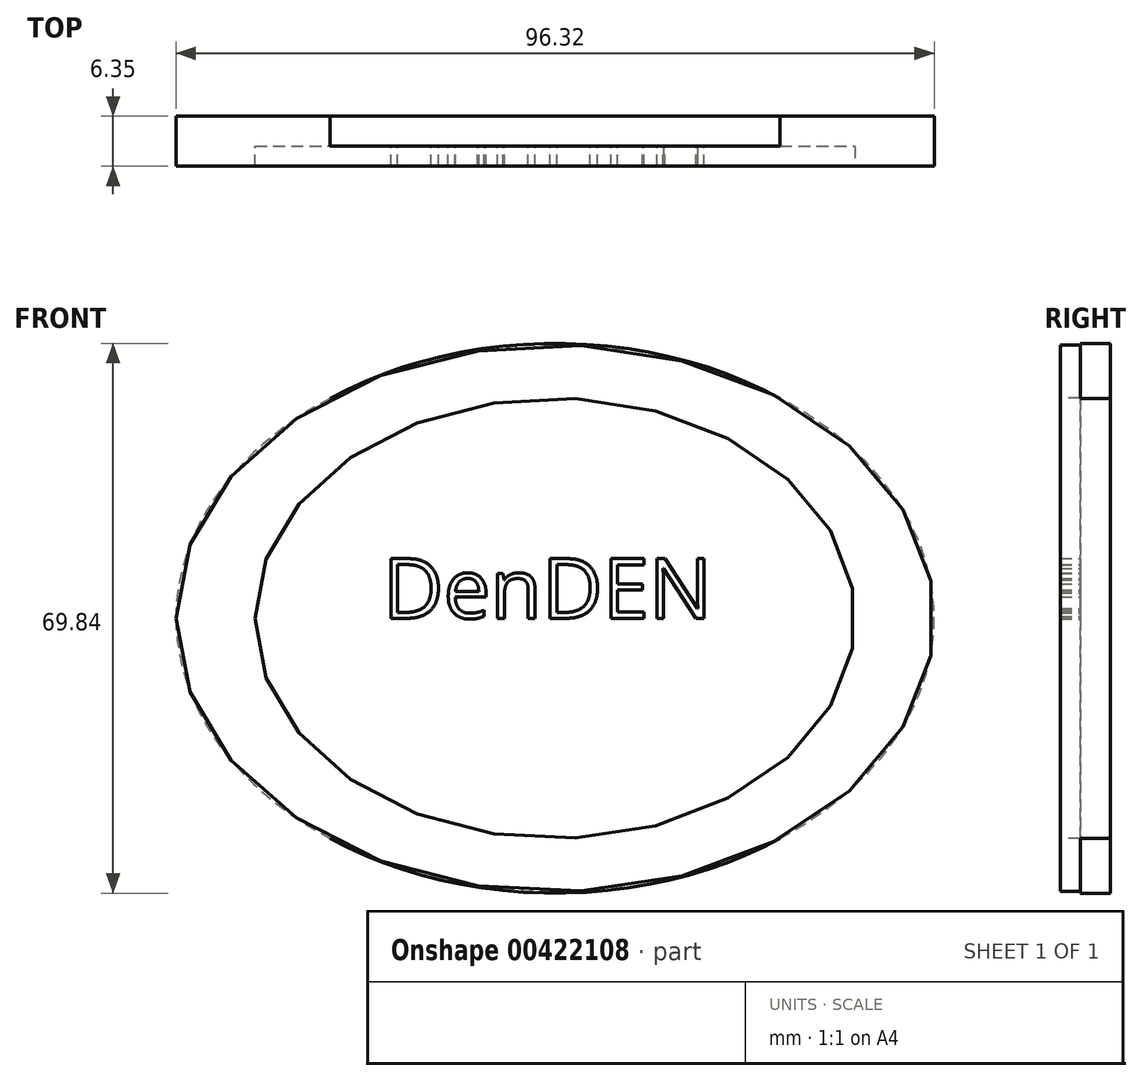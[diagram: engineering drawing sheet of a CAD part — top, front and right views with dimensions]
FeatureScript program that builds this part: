
annotation { "Feature Type Name" : "Feature", "Feature Type Description" : "" }
export const myFeature = defineFeature(function(context is Context, id is Id, definition is map)
    precondition{}
    {
        {
            var Q0;
            Q0=qCreatedBy(makeId("Front.planeOp"),FACE);
            var sketch = newSketch(context, id + "F0", { "sketchPlane" : qUnion([Q0])});
            skEllipse(sketch, "E0", {"center": v(0, 0) * mm, "majorRadius": 47.63 * mm, "minorRadius": 34.93 * mm, "majorAxis": v(-1, 0)});
            skSolve(sketch);
        }
        {
            var Q0;
            Q0=makeQuery(id+"F0.imprint","IMPRINT",FACE,{"disambiguationData":[TD([[makeQuery(id+"F0.imprint","IMPRINT",EDGE,{"derivedFrom":sQuery(id+"F0.wireOp",EDGE,"E0")}),1.0]])]});
            extrude(context, id + "F1", {"entities" : qUnion([Q0]), "depth" : 3.8 * mm});
        }
        {
            var Q0;
            Q0=makeQuery(id+"F1.opExtrude","CAP_FACE",FACE,{"disambiguationData":[OSD([sQuery(id+"F0.wireOp",EDGE,"E0")])],"isStart":false});
            var sketch = newSketch(context, id + "F2", { "sketchPlane" : qUnion([Q0])});
            skText(sketch, "E1", { "text": "DenDEN\n", "fontName": "OpenSans-Regular.ttf"});
            const initialGuessF2  = {"E1": [-0.02191, 0, 1, 0, 0.00764]};
            skSetInitialGuess(sketch, initialGuessF2);
            skSolve(sketch);
        }
        {
            var Q0;
            Q0 = qSketchRegion(id + "F2", true);
            extrude(context, id + "F3", {"entities" : qUnion([Q0]), "operationType" : NewBodyOperationType.ADD, "depth" : 2.54 * mm});
        }
        {
            var Q0;
            Q0=qCreatedBy(makeId("Front.planeOp"),FACE);
            var sketch = newSketch(context, id + "F4", { "sketchPlane" : qUnion([Q0])});
            skEllipse(sketch, "E2", {"center": v(0, 0) * mm, "majorRadius": 38.1 * mm, "minorRadius": 27.96 * mm, "majorAxis": v(-1, 0)});
            skEllipse(sketch, "E3", {"center": v(0, 0) * mm, "majorRadius": 48.16 * mm, "minorRadius": 34.71 * mm, "majorAxis": v(-1, 0)});
            skSolve(sketch);
        }
        {
            var Q0;
            Q0 = qSketchRegion(id + "F4", true);
            extrude(context, id + "F5", {"entities" : qUnion([Q0]), "operationType" : NewBodyOperationType.ADD, "depth" : 6.35 * mm});
        }
    });
